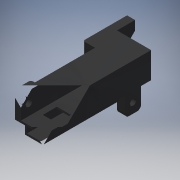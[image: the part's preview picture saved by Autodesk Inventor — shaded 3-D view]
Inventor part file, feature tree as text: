
AUTODESK INVENTOR PART (.ipt)
format: ipt  version: 2016 (Build 200138000, 138)  size: 376,320 bytes
history: native  units: mm
features: extrude x18, sketch x18, fillet x4
ambient origin geometry x8: Origin, YZ Plane, XZ Plane, XY Plane, X Axis, Y Axis, Z Axis, Center Point
bodies: Solid1 (feature_tree)
feature tree (40):
  extrude  "Extrusion1"  Depth=13.0mm
  extrude  "Extrusion2"  Depth=15.0mm
  extrude  "Extrusion3"  Depth=5.0mm
  extrude  "Extrusion7"  Depth=1.0mm TaperAngle=0.0deg
  extrude  "Extrusion9"  Depth=3.2mm
  extrude  "Extrusion10"  Depth=3.0mm
  extrude  "Extrusion11"  Depth=7.0mm
  extrude  "Extrusion15"  Depth=4.0mm
  sketch  "Sketch17"  dims[d39=10.0mm d40=0.0mm d47=1.0mm]
  fillet  "Fillet11"  Radius=8.0mm
  extrude  "Extrusion18"  Depth=1.0mm
  extrude  "Extrusion19"  Depth=1.0mm TaperAngle=0.0deg
  extrude  "Extrusion28"  Depth=5.0mm
  extrude  "Extrusion29"  TaperAngle=0.0deg  [1 undecoded]
  extrude  "Extrusion35"  Depth=15.0mm TaperAngle=0.0deg
  extrude  "Extrusion36"  Depth=8.0mm
  fillet  "Fillet20"  Radius=7.0mm
  extrude  "Extrusion37"  Depth=2.0mm
  extrude  "Extrusion38"  Depth=6.0mm TaperAngle=0.0deg
  extrude  "Extrusion39"  Depth=4.0mm
  fillet  "Fillet21"  Radius=8.0mm
  extrude  "Extrusion40"  Depth=3.0mm
  fillet  "Fillet24"  Radius=4.45mm
  sketch  "Sketch1"  dims[d2=11.0mm d3=13.0mm]
  sketch  "Sketch2"  dims[d6=13.0mm d7=15.0mm]
  sketch  "Sketch3"  dims[d8=50.0mm d9=0.0mm d10=5.0mm]
  sketch  "Sketch7"  dims[d14=1.5mm d15=1.0mm d16=0.0mm]
  sketch  "Sketch9"  dims[d17=47.0mm d18=3.2mm]
  sketch  "Sketch11"  dims[d19=50.0mm d20=0.0mm d33=3.0mm]
  sketch  "Sketch12"  dims[d34=8.0mm d35=7.0mm]
  sketch  "Sketch16"  dims[d36=4.0mm d37=4.0mm d38=8.0mm]
  sketch  "Sketch21"  dims[d48=1.0mm d49=1.0mm d50=0.0mm]
  sketch  "Sketch31"  dims[d51=7.5mm d52=5.0mm]
  sketch  "Sketch32"  dims[d53=1.0mm d54=0.0mm d55=0.0mm]
  sketch  "Sketch39"  dims[d56=3.0mm d57=15.0mm d58=0.0mm]
  sketch  "Sketch40"  dims[d75=2.0mm d76=0.0mm d78=8.0mm d92=7.0mm]
  sketch  "Sketch41"  dims[d93=5.0mm d97=2.0mm]
  sketch  "Sketch42"  dims[d98=2.0mm d99=0.0mm d108=6.0mm d109=0.0mm]
  sketch  "Sketch43"  dims[d144=4.0mm d145=4.0mm d147=8.0mm]
  sketch  "Sketch44"  dims[d150=4.45mm d151=1.4mm d153=4.45mm d154=1.4mm d155=2.0mm d156=0.0mm d160=10.0mm d162=3.5mm d164=3.0mm d165=0.0mm d218=1.0mm d219=3.0mm d220=0.0mm d221=1.0mm d222=0.0mm d224=1.0mm d226=1.0mm d227=0.0mm d230=5.0mm d231=3.0mm d232=5.0mm d233=0.0mm d234=1.0mm d235=6.0mm d236=3.5mm d237=3.0mm d238=2.0mm d239=15.0mm d240=0.0mm d241=1.0mm d242=3.0mm d243=3.0mm d244=7.0mm d245=7.0mm d246=8.0mm d247=8.0mm d250=2.0mm d251=0.0mm d252=3.0mm d253=10.3mm]
note: 1 required parameter value undecoded (feature->parameter linkage not recoverable at this tier; creation-order binding heuristic only, values carry confidence <= 0.55)
